# Revit family: 098
name_source: partatom
category: Pipe Accessories
units: mm (PartAtom-declared; Revit-internal decimal feet)

## family parameters
Always vertical = Yes
Cut with Voids When Loaded = No
OmniClass Number = 23.45.00.00
OmniClass Title = Sanitary, Laundry, and Cleaning Equipment
Part Type = Valve - Breaks Into
Round Connector Dimension = Use Diameter
Shared = No
Work Plane-Based = No

## types (1)
- 098
    Ball = Chrome-plated brass CW617N
    Body = Nickel-plated brass CW617N
    CSV = ITAP
    Description = IDEAL BALL VALVE WITH O-RING, FULL FLOW FOR MANIFOLDS
    Female end adapter = Nickel-plated brass CW617N
    Manufacturer = ITAP S.p.A.
    Model = 098S
    Nut = Nickel-plated brass CW617N
    O ring = Viton
    O-ring = NBR
    Ring = Steel
    Screw = Zinc-plated steel C4C
    Seat = P.T.F.E.
    Stem = Brass CW614N
    T handle = Varnished aluminium
    URL = https://www.itap.it
    Union = Nickel-plated brass CW617N

## geometry (parser evidence)
native form markers: Sweep x16
no freeform markers — native parametric forms only
